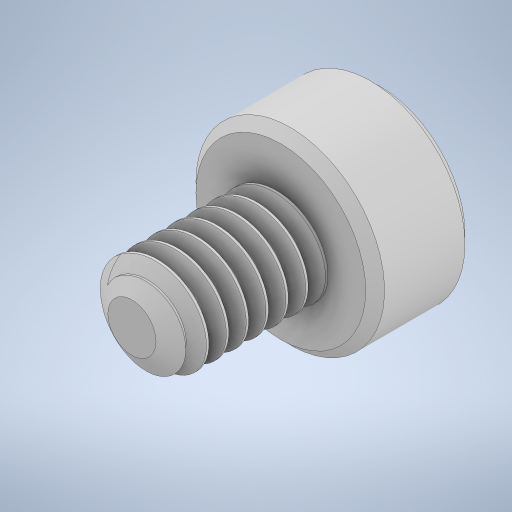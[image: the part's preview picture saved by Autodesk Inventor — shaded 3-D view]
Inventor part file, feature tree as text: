
AUTODESK INVENTOR PART (.ipt)
format: ipt  version: 2024 (Build 280153000, 153)  size: 531,456 bytes
history: native  units: mm
features: other x1, chamfer x1
ambient origin geometry x8: Origin, YZ Plane, XZ Plane, XY Plane, X Axis, Y Axis, Z Axis, Center Point
bodies: Body1 (feature_tree)
feature tree (2):
  other  "Těleso1"
  chamfer  "Chamfer1"  [1 undecoded]
note: 1 required parameter value undecoded (feature->parameter linkage not recoverable at this tier; creation-order binding heuristic only, values carry confidence <= 0.55)
